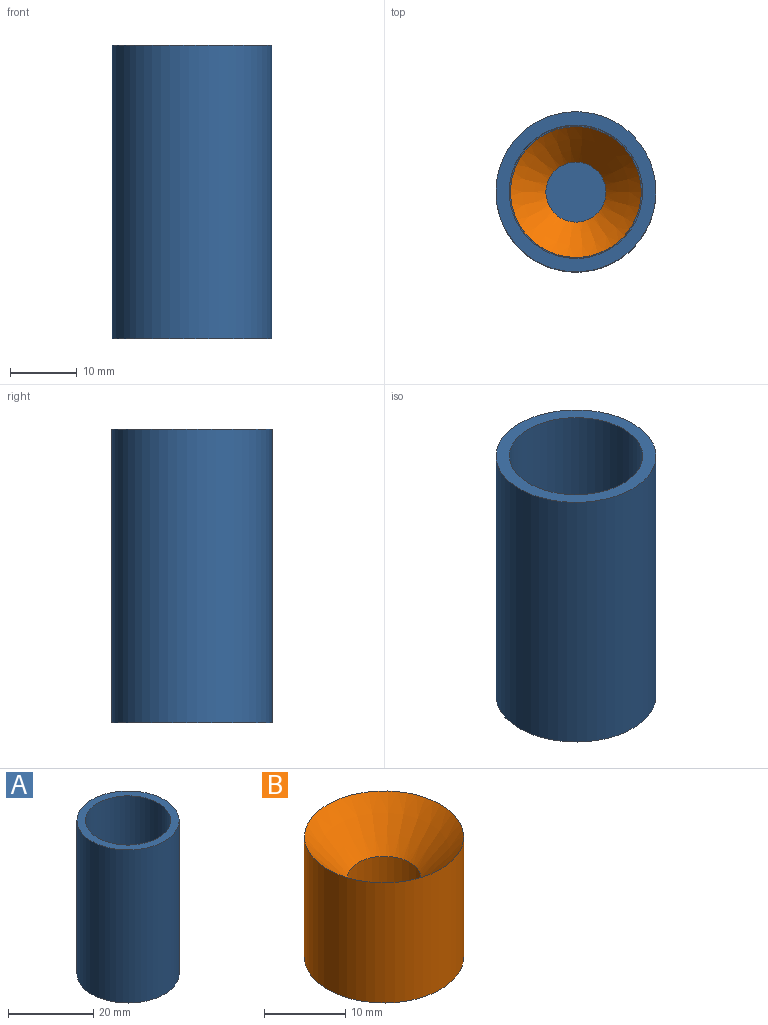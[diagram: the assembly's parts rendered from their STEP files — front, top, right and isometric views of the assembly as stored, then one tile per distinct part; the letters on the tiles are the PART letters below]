
ASSEMBLY  parts=2 mates=1
PART A: 5 faces, bbox 24x24x44 mm
  f0: cylinder r=12mm len=44mm, axis (0,0,-1), area 3317.5mm2, adj f1,f3
  f1: plane 24x24mm, normal (0,0,-1), area 452.4mm2, adj f0
  f2: cylinder r=10mm len=42mm, axis (0,0,-1), area 2638.9mm2, adj f3,f4
  f3: plane 24x24mm, normal (0,0,1), area 138.2mm2, adj f0,f2
  f4: plane 20x20mm, normal (0,0,1), area 314.2mm2, adj f2
PART B: 5 faces, bbox 19.6x19.6x18.1 mm
  f0: cylinder r=7.6mm len=15.2mm, axis (0,0,-1), area 573mm2, adj f2,f3
  f1: cylinder r=9.8mm len=19.6mm, axis (0,0,-1), area 1115.5mm2, adj f2,f4
  f2: plane 19.6x19.6mm, normal (0,0,-1), area 120.3mm2, adj f0,f1
  f3: plane 15.2x15.2mm, normal (0,0,-1), area 117.8mm2, adj f0,f4
  f4: cone r=4.5mm half-angle=40.9deg, axis (0,0,1), area 363.6mm2, adj f1,f3
PLACE A t=(-23.79,-9.05,-14.98)mm
PLACE B t=(-23.79,-9.05,-12.98)mm
MATE parallel B.f0 <-> A.f0  axis (0,0,-1) through (-23.79,-9.05,-12.98)mm
